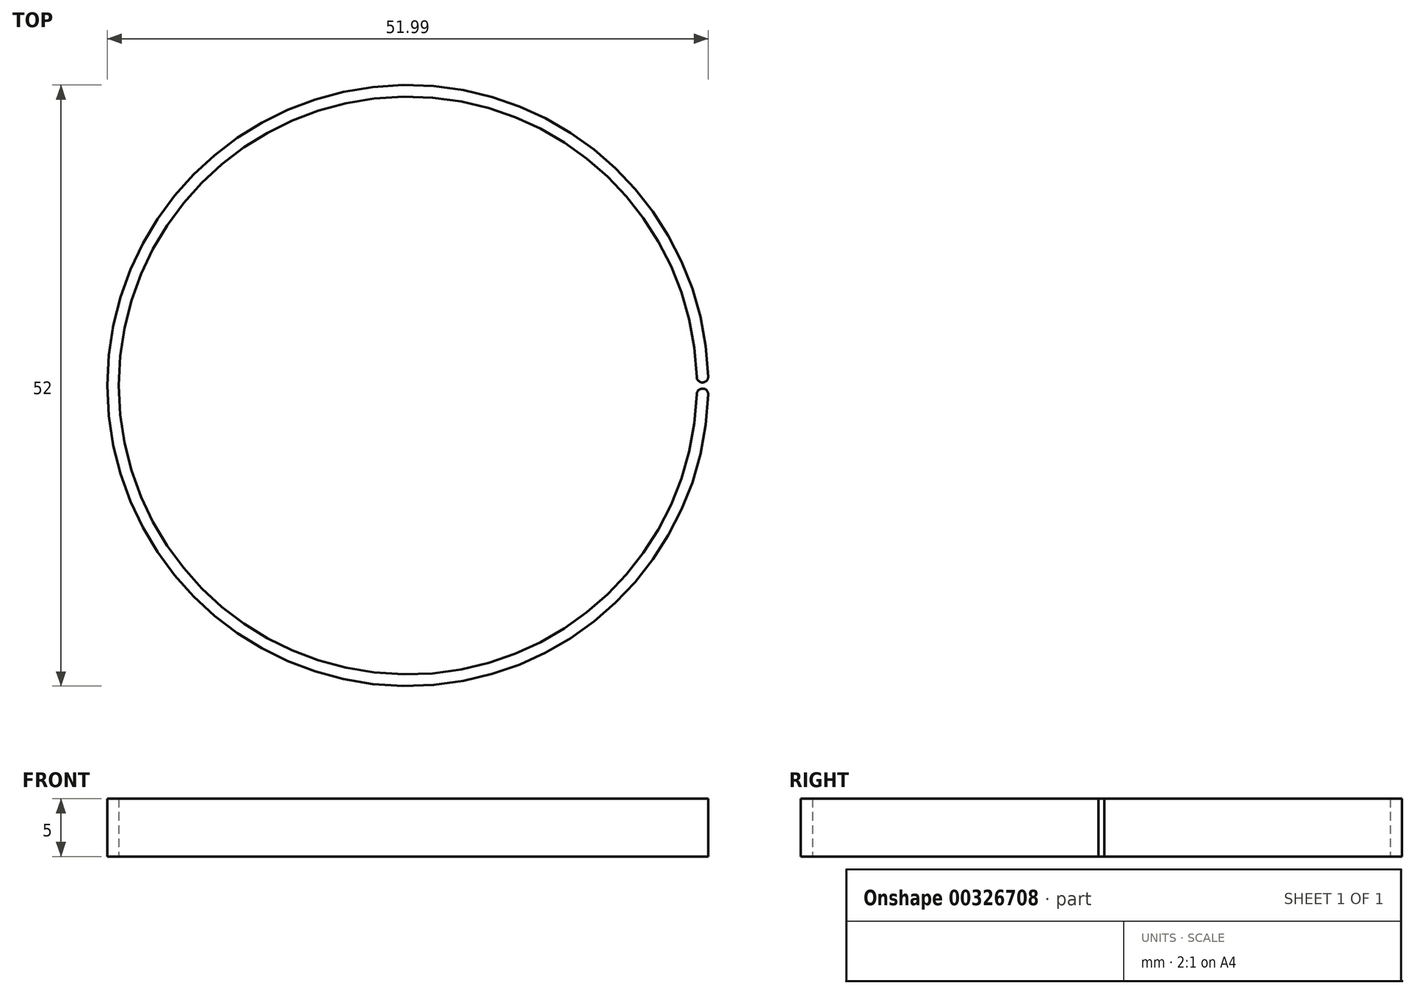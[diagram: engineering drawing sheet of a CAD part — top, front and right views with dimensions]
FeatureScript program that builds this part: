
annotation { "Feature Type Name" : "Feature", "Feature Type Description" : "" }
export const myFeature = defineFeature(function(context is Context, id is Id, definition is map)
    precondition{}
    {
        {
            var Q0;
            Q0=qCreatedBy(makeId("Top.planeOp"),FACE);
            var sketch = newSketch(context, id + "F0", { "sketchPlane" : qUnion([Q0])});
            skArc(sketch, "E0", {"start": v(24.99, 0.75) * mm, "mid": v(-25, 0) * mm, "end": v(24.99, -0.75) * mm});
            skArc(sketch, "E1.0", {"start": v(25.99, 0.78) * mm, "mid": v(-26, 0) * mm, "end": v(25.99, -0.78) * mm});
            skArc(sketch, "E2", {"start": v(25.99, -0.78) * mm, "mid": v(25.5, -0.27) * mm, "end": v(24.99, -0.75) * mm});
            skPoint(sketch, "E2.first.point", {"position": v(24.99, -0.75) * mm});
            skPoint(sketch, "E2.second.point", {"position": v(25.99, -0.78) * mm});
            skPoint(sketch, "E2.third.point", {"position": v(25.99, -0.78) * mm});
            skPoint(sketch, "E3.MirrorP", {"position": v(25.99, 0.78) * mm});
            skArc(sketch, "E4.MirrorC", {"start": v(25.99, 0.78) * mm, "mid": v(25.5, 0.27) * mm, "end": v(24.99, 0.75) * mm});
            skPoint(sketch, "E5.MirrorP", {"position": v(24.99, 0.75) * mm});
            skSolve(sketch);
        }
        {
            var Q0;
            Q0=makeQuery(id+"F0.imprint","IMPRINT",FACE,{"disambiguationData":[TD([[makeQuery(id+"F0.imprint","IMPRINT",EDGE,{"derivedFrom":sQuery(id+"F0.wireOp",EDGE,"E0")}),-1.0]])]});
            extrude(context, id + "F1", {"entities" : qUnion([Q0]), "depth" : 5 * mm});
        }
    });
